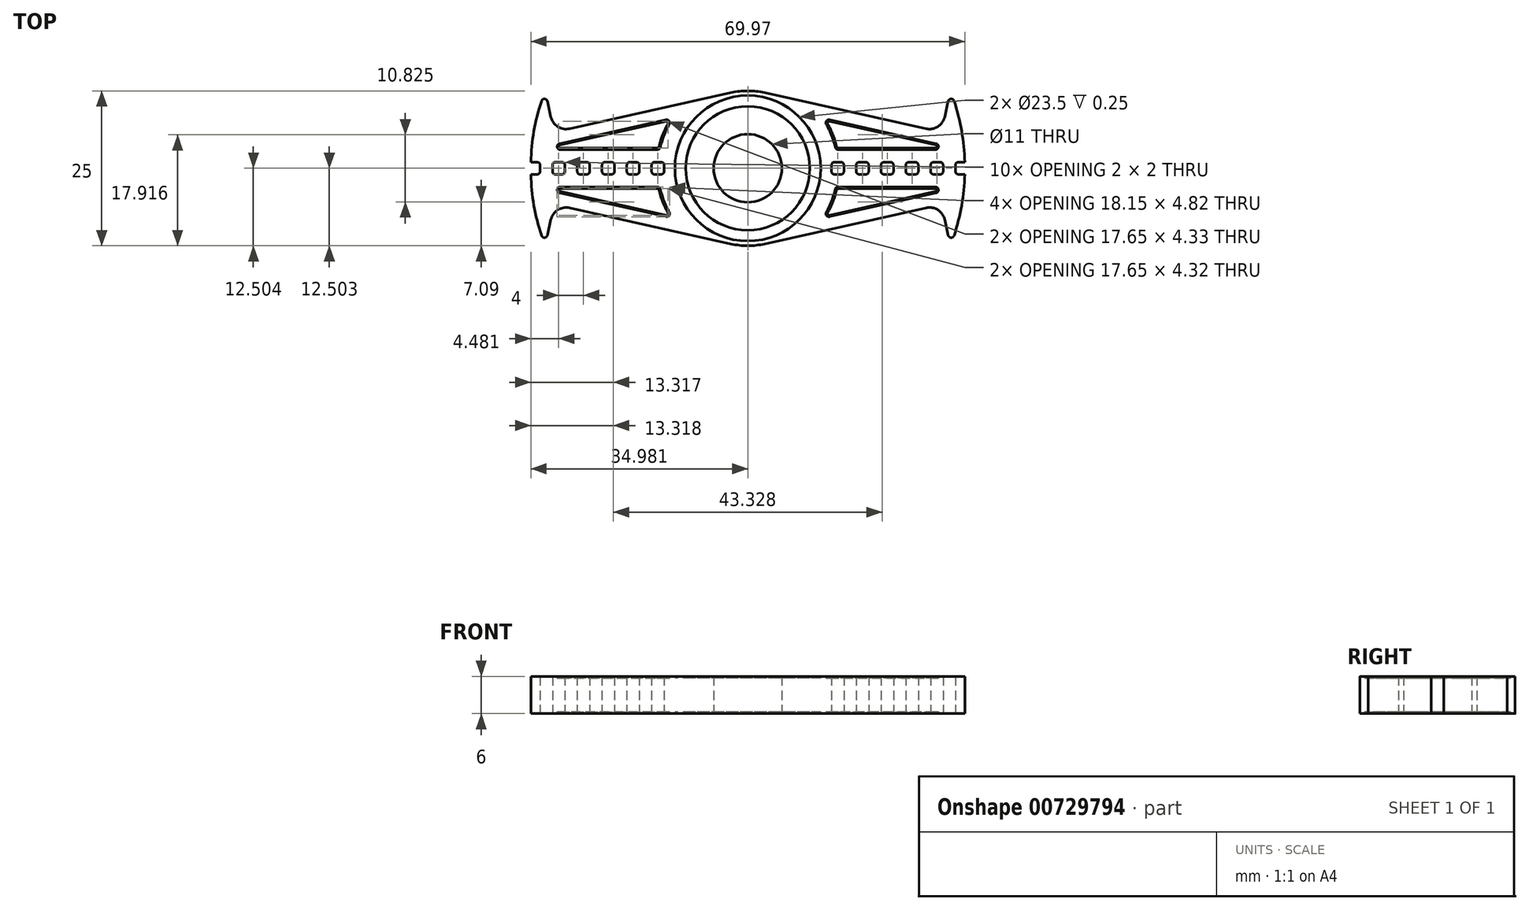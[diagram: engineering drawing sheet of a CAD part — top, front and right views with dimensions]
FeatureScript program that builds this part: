
annotation { "Feature Type Name" : "Feature", "Feature Type Description" : "" }
export const myFeature = defineFeature(function(context is Context, id is Id, definition is map)
    precondition{}
    {
        {
            var Q0;
            Q0=qCreatedBy(makeId("Top.planeOp"),FACE);
            var sketch = newSketch(context, id + "F0", { "sketchPlane" : qUnion([Q0])});
            skCircle(sketch, "E0", {"center": v(2053.21, 271.31) * mm, "radius": 9.45 * mm});
            skCircle(sketch, "E1", {"center": v(2053.21, 271.31) * mm, "radius": 5.5 * mm});
            skArc(sketch, "E2", {"start": v(2050.49, 259.11) * mm, "mid": v(2053.21, 258.81) * mm, "end": v(2055.93, 259.11) * mm});
            skLineSegment(sketch, "E3", {"start": v(2024.44, 277.7) * mm, "end": v(2050.49, 283.51) * mm});
            skLineSegment(sketch, "E4", {"start": v(2024.44, 264.92) * mm, "end": v(2050.49, 259.11) * mm});
            skLineSegment(sketch, "E5", {"start": v(2033.71, 271.81) * mm, "end": v(2033.71, 270.82) * mm});
            skLineSegment(sketch, "E6", {"start": v(2035.71, 271.81) * mm, "end": v(2035.71, 270.82) * mm});
            skLineSegment(sketch, "E7", {"start": v(2037.71, 271.82) * mm, "end": v(2037.71, 270.82) * mm});
            skLineSegment(sketch, "E8", {"start": v(2039.71, 271.82) * mm, "end": v(2039.71, 270.82) * mm});
            skLineSegment(sketch, "E9", {"start": v(2034.21, 272.31) * mm, "end": v(2035.21, 272.31) * mm});
            skLineSegment(sketch, "E10", {"start": v(2038.21, 272.32) * mm, "end": v(2039.21, 272.32) * mm});
            skLineSegment(sketch, "E11", {"start": v(2034.21, 270.32) * mm, "end": v(2035.21, 270.32) * mm});
            skLineSegment(sketch, "E12", {"start": v(2038.21, 270.32) * mm, "end": v(2039.21, 270.32) * mm});
            skLineSegment(sketch, "E13", {"start": v(2022.86, 275.3) * mm, "end": v(2040.01, 279.13) * mm});
            skLineSegment(sketch, "E14", {"start": v(2022.97, 274.31) * mm, "end": v(2038.63, 274.32) * mm});
            skArc(sketch, "E15", {"start": v(2040.56, 278.4) * mm, "mid": v(2039.7, 276.6) * mm, "end": v(2039.11, 274.7) * mm});
            skArc(sketch, "E16", {"start": v(2022.86, 275.3) * mm, "mid": v(2022.47, 274.76) * mm, "end": v(2022.97, 274.31) * mm});
            skLineSegment(sketch, "E17", {"start": v(2022.86, 267.32) * mm, "end": v(2040.01, 263.5) * mm});
            skArc(sketch, "E18", {"start": v(2039.11, 267.93) * mm, "mid": v(2039.7, 266.03) * mm, "end": v(2040.56, 264.23) * mm});
            skLineSegment(sketch, "E19", {"start": v(2022.97, 268.31) * mm, "end": v(2038.63, 268.31) * mm});
            skArc(sketch, "E20", {"start": v(2022.97, 268.31) * mm, "mid": v(2022.47, 267.87) * mm, "end": v(2022.86, 267.32) * mm});
            skCircle(sketch, "E21", {"center": v(2053.21, 271.31) * mm, "radius": 12 * mm});
            skCircle(sketch, "E22", {"center": v(2053.21, 271.31) * mm, "radius": 10 * mm});
            skArc(sketch, "E23", {"start": v(2019.94, 282.16) * mm, "mid": v(2018.73, 277.3) * mm, "end": v(2018.23, 272.31) * mm});
            skLineSegment(sketch, "E24", {"start": v(2020.9, 260.51) * mm, "end": v(2021.46, 263.03) * mm});
            skLineSegment(sketch, "E25", {"start": v(2020.9, 282.12) * mm, "end": v(2021.46, 279.6) * mm});
            skArc(sketch, "E26", {"start": v(2018.23, 270.31) * mm, "mid": v(2018.73, 265.33) * mm, "end": v(2019.94, 260.46) * mm});
            skArc(sketch, "E27", {"start": v(2021.46, 279.6) * mm, "mid": v(2022.56, 278.03) * mm, "end": v(2024.44, 277.7) * mm});
            skArc(sketch, "E28", {"start": v(2024.44, 264.92) * mm, "mid": v(2022.56, 264.6) * mm, "end": v(2021.46, 263.03) * mm});
            skArc(sketch, "E29", {"start": v(2020.9, 282.12) * mm, "mid": v(2020.43, 282.5) * mm, "end": v(2019.94, 282.16) * mm});
            skArc(sketch, "E30", {"start": v(2019.94, 260.46) * mm, "mid": v(2020.43, 260.12) * mm, "end": v(2020.9, 260.51) * mm});
            skArc(sketch, "E31", {"start": v(2040.01, 263.5) * mm, "mid": v(2040.52, 263.69) * mm, "end": v(2040.56, 264.23) * mm});
            skArc(sketch, "E32", {"start": v(2039.11, 267.93) * mm, "mid": v(2038.94, 268.2) * mm, "end": v(2038.63, 268.31) * mm});
            skArc(sketch, "E33", {"start": v(2038.63, 274.32) * mm, "mid": v(2038.94, 274.42) * mm, "end": v(2039.11, 274.7) * mm});
            skArc(sketch, "E34", {"start": v(2040.56, 278.4) * mm, "mid": v(2040.52, 278.94) * mm, "end": v(2040.01, 279.13) * mm});
            skArc(sketch, "E35", {"start": v(2038.21, 272.32) * mm, "mid": v(2037.86, 272.17) * mm, "end": v(2037.71, 271.82) * mm});
            skArc(sketch, "E36", {"start": v(2039.71, 271.82) * mm, "mid": v(2039.57, 272.17) * mm, "end": v(2039.21, 272.32) * mm});
            skArc(sketch, "E37", {"start": v(2039.21, 270.32) * mm, "mid": v(2039.57, 270.46) * mm, "end": v(2039.71, 270.82) * mm});
            skArc(sketch, "E38", {"start": v(2037.71, 270.82) * mm, "mid": v(2037.86, 270.46) * mm, "end": v(2038.21, 270.32) * mm});
            skArc(sketch, "E39", {"start": v(2035.71, 271.81) * mm, "mid": v(2035.57, 272.17) * mm, "end": v(2035.21, 272.31) * mm});
            skArc(sketch, "E40", {"start": v(2035.21, 270.32) * mm, "mid": v(2035.57, 270.46) * mm, "end": v(2035.71, 270.82) * mm});
            skArc(sketch, "E41", {"start": v(2034.21, 272.31) * mm, "mid": v(2033.86, 272.17) * mm, "end": v(2033.71, 271.81) * mm});
            skArc(sketch, "E42", {"start": v(2033.71, 270.82) * mm, "mid": v(2033.86, 270.46) * mm, "end": v(2034.21, 270.32) * mm});
            skLineSegment(sketch, "E43", {"start": v(2029.71, 271.81) * mm, "end": v(2029.71, 270.82) * mm});
            skLineSegment(sketch, "E44", {"start": v(2031.71, 271.81) * mm, "end": v(2031.71, 270.82) * mm});
            skLineSegment(sketch, "E45", {"start": v(2030.21, 272.31) * mm, "end": v(2031.21, 272.31) * mm});
            skLineSegment(sketch, "E46", {"start": v(2030.21, 270.32) * mm, "end": v(2031.21, 270.32) * mm});
            skArc(sketch, "E47", {"start": v(2031.71, 271.81) * mm, "mid": v(2031.57, 272.17) * mm, "end": v(2031.21, 272.31) * mm});
            skArc(sketch, "E48", {"start": v(2031.21, 270.32) * mm, "mid": v(2031.57, 270.46) * mm, "end": v(2031.71, 270.82) * mm});
            skArc(sketch, "E49", {"start": v(2030.21, 272.31) * mm, "mid": v(2029.86, 272.17) * mm, "end": v(2029.71, 271.81) * mm});
            skArc(sketch, "E50", {"start": v(2029.71, 270.82) * mm, "mid": v(2029.86, 270.46) * mm, "end": v(2030.21, 270.32) * mm});
            skLineSegment(sketch, "E51", {"start": v(2025.71, 271.81) * mm, "end": v(2025.71, 270.81) * mm});
            skLineSegment(sketch, "E52", {"start": v(2027.71, 271.81) * mm, "end": v(2027.71, 270.81) * mm});
            skLineSegment(sketch, "E53", {"start": v(2026.21, 272.31) * mm, "end": v(2027.21, 272.31) * mm});
            skLineSegment(sketch, "E54", {"start": v(2026.21, 270.31) * mm, "end": v(2027.21, 270.31) * mm});
            skArc(sketch, "E55", {"start": v(2027.71, 271.81) * mm, "mid": v(2027.57, 272.17) * mm, "end": v(2027.21, 272.31) * mm});
            skArc(sketch, "E56", {"start": v(2027.21, 270.31) * mm, "mid": v(2027.57, 270.46) * mm, "end": v(2027.71, 270.81) * mm});
            skArc(sketch, "E57", {"start": v(2026.21, 272.31) * mm, "mid": v(2025.86, 272.17) * mm, "end": v(2025.71, 271.81) * mm});
            skArc(sketch, "E58", {"start": v(2025.71, 270.81) * mm, "mid": v(2025.86, 270.46) * mm, "end": v(2026.21, 270.31) * mm});
            skLineSegment(sketch, "E59", {"start": v(2021.71, 271.81) * mm, "end": v(2021.71, 270.81) * mm});
            skLineSegment(sketch, "E60", {"start": v(2023.71, 271.81) * mm, "end": v(2023.71, 270.81) * mm});
            skLineSegment(sketch, "E61", {"start": v(2022.21, 272.31) * mm, "end": v(2023.21, 272.31) * mm});
            skLineSegment(sketch, "E62", {"start": v(2022.21, 270.31) * mm, "end": v(2023.21, 270.31) * mm});
            skArc(sketch, "E63", {"start": v(2023.71, 271.81) * mm, "mid": v(2023.57, 272.17) * mm, "end": v(2023.21, 272.31) * mm});
            skArc(sketch, "E64", {"start": v(2023.21, 270.31) * mm, "mid": v(2023.57, 270.46) * mm, "end": v(2023.71, 270.81) * mm});
            skArc(sketch, "E65", {"start": v(2022.21, 272.31) * mm, "mid": v(2021.86, 272.17) * mm, "end": v(2021.71, 271.81) * mm});
            skArc(sketch, "E66", {"start": v(2021.71, 270.81) * mm, "mid": v(2021.86, 270.46) * mm, "end": v(2022.21, 270.31) * mm});
            skLineSegment(sketch, "E67", {"start": v(2019.71, 271.81) * mm, "end": v(2019.71, 270.81) * mm});
            skLineSegment(sketch, "E68", {"start": v(2018.23, 272.31) * mm, "end": v(2019.21, 272.31) * mm});
            skLineSegment(sketch, "E69", {"start": v(2018.23, 270.31) * mm, "end": v(2019.21, 270.31) * mm});
            skArc(sketch, "E70", {"start": v(2019.71, 271.81) * mm, "mid": v(2019.57, 272.17) * mm, "end": v(2019.21, 272.31) * mm});
            skArc(sketch, "E71", {"start": v(2019.21, 270.31) * mm, "mid": v(2019.57, 270.46) * mm, "end": v(2019.71, 270.81) * mm});
            skLineSegment(sketch, "E72", {"start": v(2081.98, 277.7) * mm, "end": v(2055.93, 283.51) * mm});
            skLineSegment(sketch, "E73", {"start": v(2081.98, 264.92) * mm, "end": v(2055.93, 259.11) * mm});
            skLineSegment(sketch, "E74", {"start": v(2072.71, 271.81) * mm, "end": v(2072.71, 270.82) * mm});
            skLineSegment(sketch, "E75", {"start": v(2070.71, 271.81) * mm, "end": v(2070.71, 270.82) * mm});
            skLineSegment(sketch, "E76", {"start": v(2068.71, 271.82) * mm, "end": v(2068.71, 270.82) * mm});
            skLineSegment(sketch, "E77", {"start": v(2066.71, 271.82) * mm, "end": v(2066.71, 270.82) * mm});
            skLineSegment(sketch, "E78", {"start": v(2068.21, 272.32) * mm, "end": v(2067.21, 272.32) * mm});
            skLineSegment(sketch, "E79", {"start": v(2072.21, 272.31) * mm, "end": v(2071.21, 272.31) * mm});
            skLineSegment(sketch, "E80", {"start": v(2072.21, 270.32) * mm, "end": v(2071.21, 270.32) * mm});
            skLineSegment(sketch, "E81", {"start": v(2068.21, 270.32) * mm, "end": v(2067.21, 270.32) * mm});
            skLineSegment(sketch, "E82", {"start": v(2083.56, 275.3) * mm, "end": v(2066.4, 279.13) * mm});
            skLineSegment(sketch, "E83", {"start": v(2083.45, 274.31) * mm, "end": v(2067.8, 274.32) * mm});
            skArc(sketch, "E84", {"start": v(2067.31, 274.7) * mm, "mid": v(2066.71, 276.6) * mm, "end": v(2065.86, 278.4) * mm});
            skArc(sketch, "E85", {"start": v(2083.45, 274.31) * mm, "mid": v(2083.95, 274.76) * mm, "end": v(2083.56, 275.3) * mm});
            skLineSegment(sketch, "E86", {"start": v(2083.56, 267.32) * mm, "end": v(2066.4, 263.5) * mm});
            skArc(sketch, "E87", {"start": v(2065.86, 264.23) * mm, "mid": v(2066.71, 266.03) * mm, "end": v(2067.31, 267.93) * mm});
            skLineSegment(sketch, "E88", {"start": v(2083.45, 268.31) * mm, "end": v(2067.8, 268.31) * mm});
            skArc(sketch, "E89", {"start": v(2083.56, 267.32) * mm, "mid": v(2083.95, 267.87) * mm, "end": v(2083.45, 268.31) * mm});
            skLineSegment(sketch, "E90", {"start": v(2085.52, 260.51) * mm, "end": v(2084.96, 263.03) * mm});
            skLineSegment(sketch, "E91", {"start": v(2085.52, 282.12) * mm, "end": v(2084.96, 279.6) * mm});
            skArc(sketch, "E92", {"start": v(2086.49, 260.46) * mm, "mid": v(2087.7, 265.33) * mm, "end": v(2088.2, 270.31) * mm});
            skArc(sketch, "E93", {"start": v(2081.98, 277.7) * mm, "mid": v(2083.86, 278.03) * mm, "end": v(2084.96, 279.6) * mm});
            skArc(sketch, "E94", {"start": v(2084.96, 263.03) * mm, "mid": v(2083.86, 264.6) * mm, "end": v(2081.98, 264.92) * mm});
            skArc(sketch, "E95", {"start": v(2086.49, 282.16) * mm, "mid": v(2085.99, 282.5) * mm, "end": v(2085.52, 282.12) * mm});
            skArc(sketch, "E96", {"start": v(2085.52, 260.51) * mm, "mid": v(2085.99, 260.12) * mm, "end": v(2086.49, 260.46) * mm});
            skArc(sketch, "E97", {"start": v(2065.86, 264.23) * mm, "mid": v(2065.9, 263.69) * mm, "end": v(2066.4, 263.5) * mm});
            skArc(sketch, "E98", {"start": v(2067.8, 268.31) * mm, "mid": v(2067.49, 268.2) * mm, "end": v(2067.31, 267.93) * mm});
            skArc(sketch, "E99", {"start": v(2067.31, 274.7) * mm, "mid": v(2067.49, 274.42) * mm, "end": v(2067.8, 274.32) * mm});
            skArc(sketch, "E100", {"start": v(2066.4, 279.13) * mm, "mid": v(2065.9, 278.94) * mm, "end": v(2065.86, 278.4) * mm});
            skArc(sketch, "E101", {"start": v(2068.71, 271.82) * mm, "mid": v(2068.56, 272.17) * mm, "end": v(2068.21, 272.32) * mm});
            skArc(sketch, "E102", {"start": v(2067.21, 272.32) * mm, "mid": v(2066.86, 272.17) * mm, "end": v(2066.71, 271.82) * mm});
            skArc(sketch, "E103", {"start": v(2066.71, 270.82) * mm, "mid": v(2066.86, 270.46) * mm, "end": v(2067.21, 270.32) * mm});
            skArc(sketch, "E104", {"start": v(2068.21, 270.32) * mm, "mid": v(2068.56, 270.46) * mm, "end": v(2068.71, 270.82) * mm});
            skArc(sketch, "E105", {"start": v(2071.21, 272.31) * mm, "mid": v(2070.86, 272.17) * mm, "end": v(2070.71, 271.81) * mm});
            skArc(sketch, "E106", {"start": v(2070.71, 270.82) * mm, "mid": v(2070.86, 270.46) * mm, "end": v(2071.21, 270.32) * mm});
            skArc(sketch, "E107", {"start": v(2072.71, 271.81) * mm, "mid": v(2072.56, 272.17) * mm, "end": v(2072.21, 272.31) * mm});
            skArc(sketch, "E108", {"start": v(2072.21, 270.32) * mm, "mid": v(2072.56, 270.46) * mm, "end": v(2072.71, 270.82) * mm});
            skLineSegment(sketch, "E109", {"start": v(2076.71, 271.81) * mm, "end": v(2076.71, 270.82) * mm});
            skLineSegment(sketch, "E110", {"start": v(2074.71, 271.81) * mm, "end": v(2074.71, 270.82) * mm});
            skLineSegment(sketch, "E111", {"start": v(2076.21, 272.31) * mm, "end": v(2075.21, 272.31) * mm});
            skLineSegment(sketch, "E112", {"start": v(2076.21, 270.32) * mm, "end": v(2075.21, 270.32) * mm});
            skArc(sketch, "E113", {"start": v(2075.21, 272.31) * mm, "mid": v(2074.86, 272.17) * mm, "end": v(2074.71, 271.81) * mm});
            skArc(sketch, "E114", {"start": v(2074.71, 270.82) * mm, "mid": v(2074.86, 270.46) * mm, "end": v(2075.21, 270.32) * mm});
            skArc(sketch, "E115", {"start": v(2076.71, 271.81) * mm, "mid": v(2076.56, 272.17) * mm, "end": v(2076.21, 272.31) * mm});
            skArc(sketch, "E116", {"start": v(2076.21, 270.32) * mm, "mid": v(2076.56, 270.46) * mm, "end": v(2076.71, 270.82) * mm});
            skLineSegment(sketch, "E117", {"start": v(2080.71, 271.81) * mm, "end": v(2080.71, 270.81) * mm});
            skLineSegment(sketch, "E118", {"start": v(2078.71, 271.81) * mm, "end": v(2078.71, 270.81) * mm});
            skLineSegment(sketch, "E119", {"start": v(2080.21, 272.31) * mm, "end": v(2079.21, 272.31) * mm});
            skLineSegment(sketch, "E120", {"start": v(2080.21, 270.31) * mm, "end": v(2079.21, 270.31) * mm});
            skArc(sketch, "E121", {"start": v(2079.21, 272.31) * mm, "mid": v(2078.86, 272.17) * mm, "end": v(2078.71, 271.81) * mm});
            skArc(sketch, "E122", {"start": v(2078.71, 270.81) * mm, "mid": v(2078.86, 270.46) * mm, "end": v(2079.21, 270.31) * mm});
            skArc(sketch, "E123", {"start": v(2080.71, 271.81) * mm, "mid": v(2080.56, 272.17) * mm, "end": v(2080.21, 272.31) * mm});
            skArc(sketch, "E124", {"start": v(2080.21, 270.31) * mm, "mid": v(2080.56, 270.46) * mm, "end": v(2080.71, 270.81) * mm});
            skLineSegment(sketch, "E125", {"start": v(2084.71, 271.81) * mm, "end": v(2084.71, 270.81) * mm});
            skLineSegment(sketch, "E126", {"start": v(2082.71, 271.81) * mm, "end": v(2082.71, 270.81) * mm});
            skLineSegment(sketch, "E127", {"start": v(2084.21, 272.31) * mm, "end": v(2083.21, 272.31) * mm});
            skLineSegment(sketch, "E128", {"start": v(2084.21, 270.31) * mm, "end": v(2083.21, 270.31) * mm});
            skArc(sketch, "E129", {"start": v(2083.21, 272.31) * mm, "mid": v(2082.86, 272.17) * mm, "end": v(2082.71, 271.81) * mm});
            skArc(sketch, "E130", {"start": v(2082.71, 270.81) * mm, "mid": v(2082.86, 270.46) * mm, "end": v(2083.21, 270.31) * mm});
            skArc(sketch, "E131", {"start": v(2084.71, 271.81) * mm, "mid": v(2084.56, 272.17) * mm, "end": v(2084.21, 272.31) * mm});
            skArc(sketch, "E132", {"start": v(2084.21, 270.31) * mm, "mid": v(2084.56, 270.46) * mm, "end": v(2084.71, 270.81) * mm});
            skLineSegment(sketch, "E133", {"start": v(2086.71, 271.81) * mm, "end": v(2086.71, 270.81) * mm});
            skLineSegment(sketch, "E134", {"start": v(2088.2, 270.31) * mm, "end": v(2087.21, 270.31) * mm});
            skArc(sketch, "E135", {"start": v(2087.21, 272.31) * mm, "mid": v(2086.86, 272.17) * mm, "end": v(2086.71, 271.81) * mm});
            skArc(sketch, "E136", {"start": v(2086.71, 270.81) * mm, "mid": v(2086.86, 270.46) * mm, "end": v(2087.21, 270.31) * mm});
            skLineSegment(sketch, "E137", {"start": v(2088.2, 272.31) * mm, "end": v(2087.21, 272.31) * mm});
            skArc(sketch, "E138", {"start": v(2088.2, 272.31) * mm, "mid": v(2087.7, 277.3) * mm, "end": v(2086.49, 282.16) * mm});
            skArc(sketch, "E139", {"start": v(2055.93, 283.51) * mm, "mid": v(2053.21, 283.81) * mm, "end": v(2050.49, 283.51) * mm});
            skLineSegment(sketch, "E140", {"start": v(2022.92, 275.06) * mm, "end": v(2040.07, 278.88) * mm});
            skArc(sketch, "E141", {"start": v(2022.92, 275.06) * mm, "mid": v(2022.72, 274.79) * mm, "end": v(2022.97, 274.56) * mm});
            skLineSegment(sketch, "E142", {"start": v(2022.97, 274.56) * mm, "end": v(2038.63, 274.57) * mm});
            skArc(sketch, "E143", {"start": v(2040.34, 278.52) * mm, "mid": v(2039.48, 276.69) * mm, "end": v(2038.87, 274.76) * mm});
            skArc(sketch, "E144", {"start": v(2040.34, 278.52) * mm, "mid": v(2040.32, 278.79) * mm, "end": v(2040.07, 278.88) * mm});
            skArc(sketch, "E145", {"start": v(2038.63, 274.57) * mm, "mid": v(2038.78, 274.62) * mm, "end": v(2038.87, 274.76) * mm});
            skCircle(sketch, "E146", {"center": v(2053.21, 271.31) * mm, "radius": 11.75 * mm});
            skCircle(sketch, "E147", {"center": v(2053.21, 271.31) * mm, "radius": 10.25 * mm});
            skLineSegment(sketch, "E148", {"start": v(2022.97, 268.06) * mm, "end": v(2038.63, 268.06) * mm});
            skArc(sketch, "E149", {"start": v(2022.97, 268.06) * mm, "mid": v(2022.72, 267.84) * mm, "end": v(2022.92, 267.57) * mm});
            skLineSegment(sketch, "E150", {"start": v(2022.92, 267.57) * mm, "end": v(2040.07, 263.74) * mm});
            skArc(sketch, "E151", {"start": v(2040.07, 263.74) * mm, "mid": v(2040.32, 263.84) * mm, "end": v(2040.34, 264.1) * mm});
            skArc(sketch, "E152", {"start": v(2038.87, 267.87) * mm, "mid": v(2039.48, 265.94) * mm, "end": v(2040.34, 264.1) * mm});
            skArc(sketch, "E153", {"start": v(2038.87, 267.87) * mm, "mid": v(2038.78, 268) * mm, "end": v(2038.63, 268.06) * mm});
            skArc(sketch, "E154", {"start": v(2067.8, 268.06) * mm, "mid": v(2067.64, 268) * mm, "end": v(2067.55, 267.87) * mm});
            skArc(sketch, "E155", {"start": v(2066.08, 264.1) * mm, "mid": v(2066.95, 265.94) * mm, "end": v(2067.55, 267.87) * mm});
            skArc(sketch, "E156", {"start": v(2066.08, 264.1) * mm, "mid": v(2066.1, 263.84) * mm, "end": v(2066.36, 263.74) * mm});
            skLineSegment(sketch, "E157", {"start": v(2083.5, 267.57) * mm, "end": v(2066.36, 263.74) * mm});
            skLineSegment(sketch, "E158", {"start": v(2083.45, 268.06) * mm, "end": v(2067.8, 268.06) * mm});
            skArc(sketch, "E159", {"start": v(2083.5, 267.57) * mm, "mid": v(2083.7, 267.84) * mm, "end": v(2083.45, 268.06) * mm});
            skArc(sketch, "E160", {"start": v(2083.45, 274.56) * mm, "mid": v(2083.7, 274.79) * mm, "end": v(2083.5, 275.06) * mm});
            skLineSegment(sketch, "E161", {"start": v(2083.45, 274.56) * mm, "end": v(2067.8, 274.57) * mm});
            skArc(sketch, "E162", {"start": v(2067.55, 274.76) * mm, "mid": v(2067.64, 274.62) * mm, "end": v(2067.8, 274.57) * mm});
            skArc(sketch, "E163", {"start": v(2067.55, 274.76) * mm, "mid": v(2066.95, 276.69) * mm, "end": v(2066.08, 278.52) * mm});
            skArc(sketch, "E164", {"start": v(2066.36, 278.88) * mm, "mid": v(2066.1, 278.79) * mm, "end": v(2066.08, 278.52) * mm});
            skLineSegment(sketch, "E165", {"start": v(2083.5, 275.06) * mm, "end": v(2066.36, 278.88) * mm});
            skSolve(sketch);
        }
        {
            var Q0;
            Q0 = qSketchRegion(id + "F0", true);
            var Q1;
            Q1=makeQuery(id+"F0.imprint","IMPRINT",FACE,{"disambiguationData":[TD([[makeQuery(id+"F0.imprint","IMPRINT",EDGE,{"derivedFrom":sQuery(id+"F0.wireOp",EDGE,"E160")}),1.0]])]});
            var Q2;
            Q2=makeQuery(id+"F0.imprint","IMPRINT",FACE,{"disambiguationData":[TD([[makeQuery(id+"F0.imprint","IMPRINT",EDGE,{"derivedFrom":sQuery(id+"F0.wireOp",EDGE,"E154")}),1.0]])]});
            var Q3;
            Q3=makeQuery(id+"F0.imprint","IMPRINT",FACE,{"disambiguationData":[TD([[makeQuery(id+"F0.imprint","IMPRINT",EDGE,{"derivedFrom":sQuery(id+"F0.wireOp",EDGE,"E148")}),-1.0]])]});
            var Q4;
            Q4=makeQuery(id+"F0.imprint","IMPRINT",FACE,{"disambiguationData":[TD([[makeQuery(id+"F0.imprint","IMPRINT",EDGE,{"derivedFrom":sQuery(id+"F0.wireOp",EDGE,"E140")}),-1.0]])]});
            var Q5;
            Q5=makeQuery(id+"F0.imprint","IMPRINT",FACE,{"disambiguationData":[TD([[makeQuery(id+"F0.imprint","IMPRINT",EDGE,{"derivedFrom":sQuery(id+"F0.wireOp",EDGE,"E1")}),-1.0]])]});
            var Q6;
            Q6=makeQuery(id+"F0.imprint","IMPRINT",FACE,{"disambiguationData":[TD([[makeQuery(id+"F0.imprint","IMPRINT",EDGE,{"derivedFrom":sQuery(id+"F0.wireOp",EDGE,"E146")}),-1.0]])]});
            var Q7;
            Q7=makeQuery(id+"F0.imprint","IMPRINT",FACE,{"disambiguationData":[TD([[makeQuery(id+"F0.imprint","IMPRINT",EDGE,{"derivedFrom":sQuery(id+"F0.wireOp",EDGE,"E0")}),-1.0]])]});
            extrude(context, id + "F1", {"entities" : qUnion([Q0, Q1, Q2, Q3, Q4, Q5, Q6, Q7]), "endBound" : BoundingType.SYMMETRIC, "depth" : 6 * mm, "offsetDistance" : 25 * mm});
        }
        {
            var Q0;
            Q0=qCreatedBy(makeId("Top.planeOp"),FACE);
            var sketch = newSketch(context, id + "F2", { "sketchPlane" : qUnion([Q0])});
            skArc(sketch, "E166.0", {"start": v(2022.86, 275.3) * mm, "mid": v(2022.47, 274.76) * mm, "end": v(2022.97, 274.31) * mm});
            skLineSegment(sketch, "E167.0", {"start": v(2022.86, 275.3) * mm, "end": v(2040.01, 279.13) * mm});
            skLineSegment(sketch, "E168.0", {"start": v(2022.97, 274.31) * mm, "end": v(2038.63, 274.32) * mm});
            skArc(sketch, "E169.0", {"start": v(2038.63, 274.32) * mm, "mid": v(2038.94, 274.42) * mm, "end": v(2039.11, 274.7) * mm});
            skArc(sketch, "E170.0", {"start": v(2040.56, 278.4) * mm, "mid": v(2039.7, 276.6) * mm, "end": v(2039.11, 274.7) * mm});
            skArc(sketch, "E171.0", {"start": v(2040.56, 278.4) * mm, "mid": v(2040.52, 278.94) * mm, "end": v(2040.01, 279.13) * mm});
            skLineSegment(sketch, "E172", {"start": v(2053.21, 271.31) * mm, "end": v(2019.71, 271.31) * mm, "construction": true});
            skLineSegment(sketch, "E173", {"start": v(2053.21, 271.31) * mm, "end": v(2053.21, 283.81) * mm, "construction": true});
            skArc(sketch, "E174.MirrorCS", {"start": v(2040.56, 264.23) * mm, "mid": v(2040.52, 263.69) * mm, "end": v(2040.01, 263.5) * mm});
            skArc(sketch, "E175.MirrorCS", {"start": v(2038.63, 268.31) * mm, "mid": v(2038.94, 268.2) * mm, "end": v(2039.11, 267.93) * mm});
            skArc(sketch, "E176.MirrorCS", {"start": v(2022.86, 267.33) * mm, "mid": v(2022.47, 267.87) * mm, "end": v(2022.97, 268.31) * mm});
            skArc(sketch, "E177.MirrorCS", {"start": v(2040.56, 264.23) * mm, "mid": v(2039.7, 266.03) * mm, "end": v(2039.11, 267.93) * mm});
            skLineSegment(sketch, "E178.MirrorCS", {"start": v(2022.97, 268.31) * mm, "end": v(2038.63, 268.31) * mm});
            skLineSegment(sketch, "E179.MirrorCS", {"start": v(2022.86, 267.33) * mm, "end": v(2040.01, 263.5) * mm});
            skArc(sketch, "E180.MirrorCS", {"start": v(2065.86, 278.4) * mm, "mid": v(2065.9, 278.94) * mm, "end": v(2066.4, 279.13) * mm});
            skArc(sketch, "E181.MirrorCS", {"start": v(2067.8, 274.32) * mm, "mid": v(2067.49, 274.42) * mm, "end": v(2067.31, 274.7) * mm});
            skArc(sketch, "E182.MirrorCS", {"start": v(2083.56, 275.3) * mm, "mid": v(2083.95, 274.76) * mm, "end": v(2083.45, 274.31) * mm});
            skArc(sketch, "E183.MirrorCS", {"start": v(2065.86, 264.23) * mm, "mid": v(2065.9, 263.69) * mm, "end": v(2066.41, 263.5) * mm});
            skArc(sketch, "E184.MirrorCS", {"start": v(2067.8, 268.31) * mm, "mid": v(2067.49, 268.2) * mm, "end": v(2067.31, 267.93) * mm});
            skArc(sketch, "E185.MirrorCS", {"start": v(2083.56, 267.33) * mm, "mid": v(2083.95, 267.87) * mm, "end": v(2083.45, 268.31) * mm});
            skArc(sketch, "E186.MirrorCS", {"start": v(2065.86, 278.4) * mm, "mid": v(2066.71, 276.6) * mm, "end": v(2067.31, 274.7) * mm});
            skLineSegment(sketch, "E187.MirrorCS", {"start": v(2083.45, 274.31) * mm, "end": v(2067.8, 274.32) * mm});
            skLineSegment(sketch, "E188.MirrorCS", {"start": v(2083.56, 275.3) * mm, "end": v(2066.4, 279.13) * mm});
            skLineSegment(sketch, "E189.MirrorCS", {"start": v(2083.56, 267.33) * mm, "end": v(2066.41, 263.5) * mm});
            skArc(sketch, "E190.MirrorCS", {"start": v(2065.86, 264.23) * mm, "mid": v(2066.71, 266.03) * mm, "end": v(2067.31, 267.93) * mm});
            skLineSegment(sketch, "E191.MirrorCS", {"start": v(2083.45, 268.31) * mm, "end": v(2067.8, 268.31) * mm});
            skCircle(sketch, "E192.0", {"center": v(2053.21, 271.31) * mm, "radius": 12 * mm});
            skCircle(sketch, "E193.0", {"center": v(2053.21, 271.31) * mm, "radius": 10 * mm});
            skSolve(sketch);
        }
        {
            var Q0;
            Q0 = qSketchRegion(id + "F2", true);
            extrude(context, id + "F3", {"entities" : qUnion([Q0]), "operationType" : NewBodyOperationType.ADD, "endBound" : BoundingType.SYMMETRIC, "depth" : 5.5 * mm, "offsetDistance" : 25 * mm});
        }
    });
